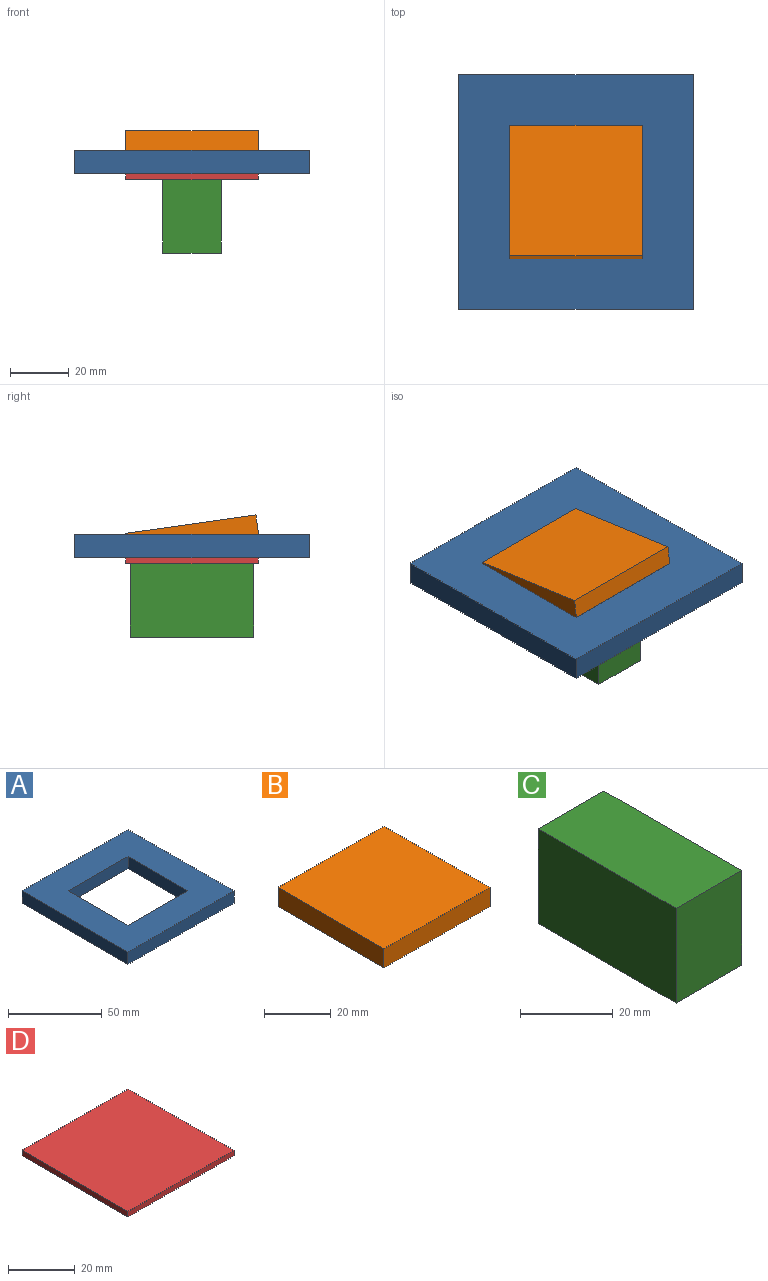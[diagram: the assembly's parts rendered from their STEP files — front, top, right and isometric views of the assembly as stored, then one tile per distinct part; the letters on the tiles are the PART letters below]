
ASSEMBLY  parts=4 mates=3
PART A: 10 faces, bbox 80x80x8 mm
  f0: plane 80x8mm, normal (0,-1,0), area 640mm2, adj f1,f7,f8,f9
  f1: plane 80x8mm, normal (1,0,0), area 640mm2, adj f0,f2,f8,f9
  f2: plane 80x8mm, normal (0,1,0), area 640mm2, adj f1,f7,f8,f9
  f3: plane 45x8mm, normal (-1,0,0), area 360mm2, adj f4,f6,f8,f9
  f4: plane 45x8mm, normal (0,1,0), area 360mm2, adj f3,f5,f8,f9
  f5: plane 45x8mm, normal (1,0,0), area 360mm2, adj f4,f6,f8,f9
  f6: plane 45x8mm, normal (0,-1,0), area 360mm2, adj f3,f5,f8,f9
  f7: plane 80x8mm, normal (-1,0,0), area 640mm2, adj f0,f2,f8,f9
  f8: plane 80x80mm, normal (0,0,1), area 4375mm2, adj f0,f1,f2,f3,f4,f5,f6,f7
  f9: plane 80x80mm, normal (0,0,-1), area 4375mm2, adj f0,f1,f2,f3,f4,f5,f6,f7
PART B: 6 faces, bbox 45x45x7 mm
  f0: plane 45x7mm, normal (1,0,0), area 315mm2, adj f1,f3,f4,f5
  f1: plane 45x7mm, normal (0,1,0), area 315mm2, adj f0,f2,f4,f5
  f2: plane 45x7mm, normal (-1,0,0), area 315mm2, adj f1,f3,f4,f5
  f3: plane 45x7mm, normal (0,-1,0), area 315mm2, adj f0,f2,f4,f5
  f4: plane 45x45mm, normal (0,0,1), area 2025mm2, adj f0,f1,f2,f3
  f5: plane 45x45mm, normal (0,0,-1), area 2025mm2, adj f0,f1,f2,f3
PART C: 6 faces, bbox 20x42x25 mm
  f0: plane 42x25mm, normal (1,0,0), area 1050mm2, adj f1,f3,f4,f5
  f1: plane 25x20mm, normal (0,1,0), area 500mm2, adj f0,f2,f4,f5
  f2: plane 42x25mm, normal (-1,0,0), area 1050mm2, adj f1,f3,f4,f5
  f3: plane 25x20mm, normal (0,-1,0), area 500mm2, adj f0,f2,f4,f5
  f4: plane 42x20mm, normal (0,0,-1), area 840mm2, adj f0,f1,f2,f3
  f5: plane 42x20mm, normal (0,0,1), area 840mm2, adj f0,f1,f2,f3
PART D: 6 faces, bbox 45x45x2 mm
  f0: plane 45x2mm, normal (0,-1,0), area 90mm2, adj f1,f3,f4,f5
  f1: plane 45x2mm, normal (1,0,0), area 90mm2, adj f0,f2,f4,f5
  f2: plane 45x2mm, normal (0,1,0), area 90mm2, adj f1,f3,f4,f5
  f3: plane 45x2mm, normal (-1,0,0), area 90mm2, adj f0,f2,f4,f5
  f4: plane 45x45mm, normal (0,0,-1), area 2025mm2, adj f0,f1,f2,f3
  f5: plane 45x45mm, normal (0,0,1), area 2025mm2, adj f0,f1,f2,f3
PLACE A at identity fixed
PLACE B rot(axis=(-1,0,0),8deg) t=(0,-0.49,4.53)mm
PLACE C t=(0,0,-2)mm
PLACE D at identity
MATE fastened D.f2 <-> A.f6  axis (0,1,0) through (0,22.5,0)mm
MATE fastened C.f5 <-> D.f4  axis (0,0,1) through (0,0,-2)mm
MATE revolute A.f5 <-> B.f2  axis (1,0,0) through (-22.5,0,8)mm
